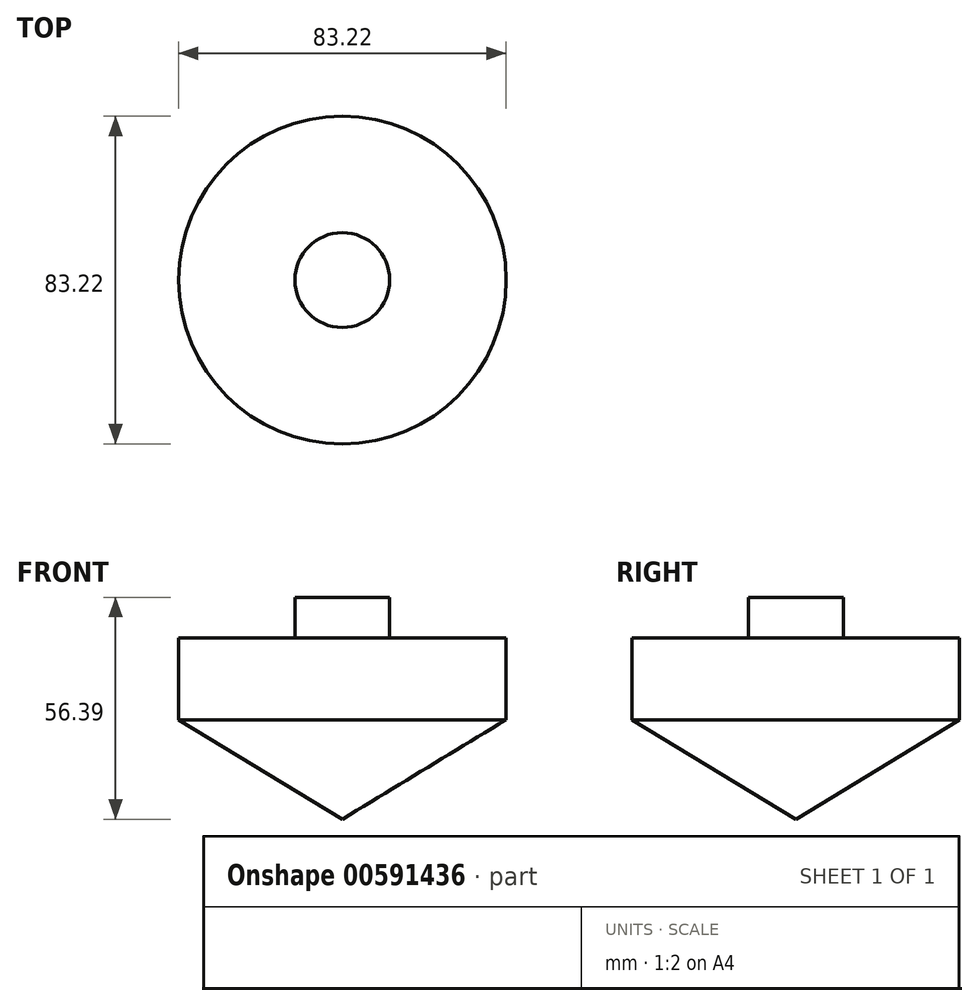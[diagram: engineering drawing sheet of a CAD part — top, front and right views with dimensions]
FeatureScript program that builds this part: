
annotation { "Feature Type Name" : "Feature", "Feature Type Description" : "" }
export const myFeature = defineFeature(function(context is Context, id is Id, definition is map)
    precondition{}
    {
        {
            var Q0;
            Q0=qCreatedBy(makeId("Front.planeOp"),FACE);
            var sketch = newSketch(context, id + "F0", { "sketchPlane" : qUnion([Q0])});
            skLineSegment(sketch, "E0", {"start": v(0, 0) * mm, "end": v(41.6, 25.3) * mm});
            skLineSegment(sketch, "E1", {"start": v(41.6, 25.3) * mm, "end": v(41.6, 46.02) * mm});
            skLineSegment(sketch, "E2", {"start": v(41.6, 46.02) * mm, "end": v(12.04, 46.02) * mm});
            skLineSegment(sketch, "E3", {"start": v(12.04, 46.02) * mm, "end": v(12.04, 56.39) * mm});
            skLineSegment(sketch, "E4", {"start": v(12.04, 56.39) * mm, "end": v(0, 56.39) * mm});
            skLineSegment(sketch, "E5", {"start": v(0, 56.39) * mm, "end": v(0, 0) * mm});
            skSolve(sketch);
        }
        {
            var Q0;
            Q0 = qSketchRegion(id + "F0", true);
            var Q1;
            Q1=sQuery(id+"F0.wireOp",EDGE,"E5");
            revolve(context, id + "F1", {"entities" : qUnion([Q0]), "axis" : qUnion([Q1]), "revolveType" : RevolveType.FULL});
        }
    });
